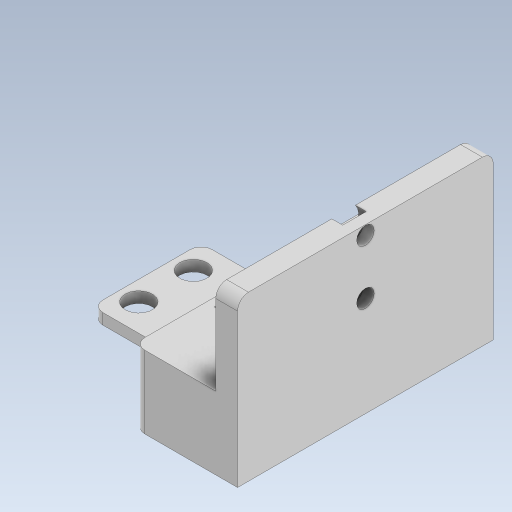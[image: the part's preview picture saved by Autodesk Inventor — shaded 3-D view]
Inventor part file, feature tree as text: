
AUTODESK INVENTOR PART (.ipt)
format: ipt  version: 2023.5 (Build 275446000, 446)  size: 396,288 bytes
history: native  units: mm
features: extrude x6, sketch x2, fillet x2
ambient origin geometry x8: Origin, YZ Plane, XZ Plane, XY Plane, X Axis, Y Axis, Z Axis, Center Point
bodies: Solid1 (feature_tree)
feature tree (10):
  sketch  "Sketch1"  dims[d2=12.0mm d3=22.875mm]
  extrude  "Extrusion1"  Depth=22.875mm
  extrude  "Extrusion2"  Depth=32.3mm
  extrude  "Extrusion3"  Depth=10.0mm
  fillet  "Fillet1"  Radius=6.0mm
  extrude  "Extrusion4"  Depth=10.0mm
  sketch  "Sketch2"  dims[d4=12.0mm d5=32.3mm d6=5.0mm d7=6.0mm d8=5.0mm d9=22.8mm d10=15.0mm d11=35.0mm d12=10.8mm d13=0.0mm d14=13.3mm d15=0.0mm d17=5.0mm d18=15.0mm d19=6.4mm d20=5.0mm d21=10.0mm d22=5.0mm d23=10.0mm d25=5.0mm d27=10.0mm d28=2.0mm d29=0.0mm d30=2.0mm d31=4.0mm d32=30.0mm d33=0.0mm d34=3.2mm d35=5.5mm d36=3.2mm d37=5.5mm d39=5.0mm d40=10.0mm d41=4.0mm d42=0.0mm d43=2.0mm d44=0.0mm d45=2.0mm d46=10.0mm]
  extrude  "Extrusion5"  Depth=10.0mm
  extrude  "Extrusion6"  Depth=15.0mm
  fillet  "Fillet2"  Radius=35.0mm
